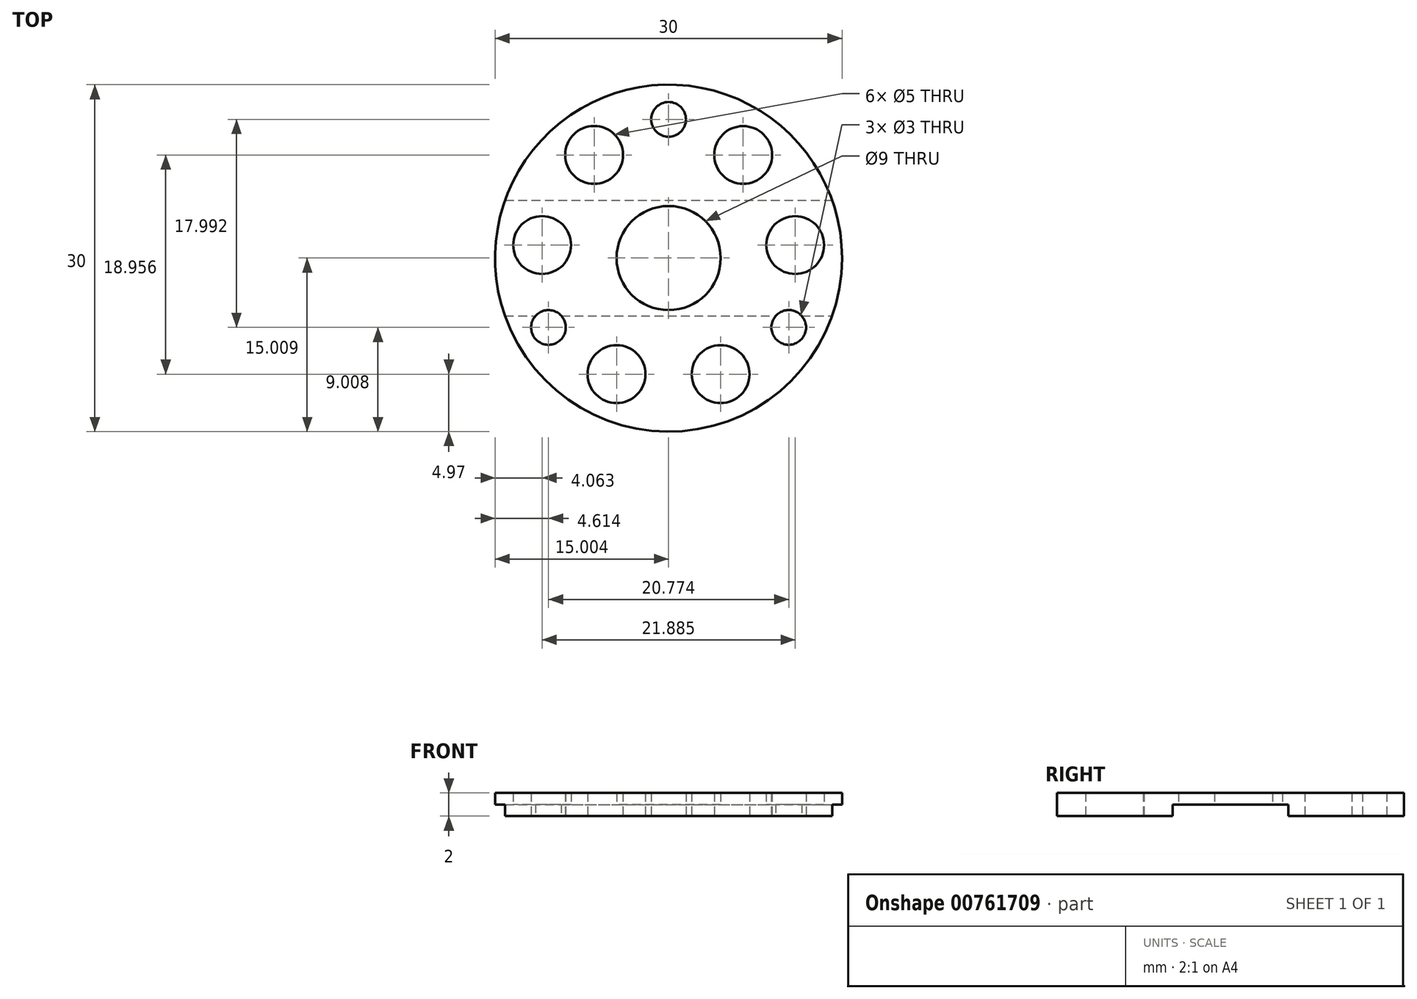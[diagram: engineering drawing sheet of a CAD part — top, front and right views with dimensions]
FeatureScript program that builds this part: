
annotation { "Feature Type Name" : "Feature", "Feature Type Description" : "" }
export const myFeature = defineFeature(function(context is Context, id is Id, definition is map)
    precondition{}
    {
        {
            var Q0;
            Q0=qCreatedBy(makeId("Top.planeOp"),FACE);
            var sketch = newSketch(context, id + "F0", { "sketchPlane" : qUnion([Q0])});
            skCircle(sketch, "E0", {"center": v(0, 0) * mm, "radius": 15 * mm});
            skArc(sketch, "E1", {"start": v(9.57, -7.24) * mm, "mid": v(10.4, -6) * mm, "end": v(11.06, -4.65) * mm, "construction": true});
            skArc(sketch, "E2", {"start": v(4.5, -10.03) * mm, "mid": v(5.6, -9.45) * mm, "end": v(6.65, -8.75) * mm, "construction": true});
            skCircle(sketch, "E3", {"center": v(0, 12) * mm, "radius": 1.5 * mm});
            skCircle(sketch, "E4.1.0", {"center": v(-10.39, -6) * mm, "radius": 1.5 * mm});
            skCircle(sketch, "E4.2.0", {"center": v(10.39, -6) * mm, "radius": 1.5 * mm});
            skLineSegment(sketch, "E4.anchor1", {"start": v(0, 0) * mm, "end": v(0, 12) * mm, "construction": true});
            skLineSegment(sketch, "E4.anchor2", {"start": v(0, 0) * mm, "end": v(3.9, -2.24) * mm, "construction": true});
            skCircle(sketch, "E5", {"center": v(4.5, -10.03) * mm, "radius": 2.5 * mm});
            skCircle(sketch, "E6", {"center": v(-4.5, -10.03) * mm, "radius": 2.5 * mm});
            skLineSegment(sketch, "E7", {"start": v(-4.5, -10.03) * mm, "end": v(-2, -10.03) * mm, "construction": true});
            skCircle(sketch, "E8.1.0", {"center": v(6.45, 8.92) * mm, "radius": 2.5 * mm});
            skCircle(sketch, "E8.1.1", {"center": v(10.95, 1.13) * mm, "radius": 2.5 * mm});
            skCircle(sketch, "E8.2.0", {"center": v(-10.94, 1.14) * mm, "radius": 2.5 * mm});
            skCircle(sketch, "E8.2.1", {"center": v(-6.44, 8.93) * mm, "radius": 2.5 * mm});
            skCircle(sketch, "E9", {"center": v(0, 0) * mm, "radius": 4.5 * mm});
            skLineSegment(sketch, "E10.trimOffspring", {"start": v(2, -10.03) * mm, "end": v(4.5, -10.03) * mm, "construction": true});
            skArc(sketch, "E11.trimOffspring", {"start": v(8.94, -6.4) * mm, "mid": v(9.52, -5.5) * mm, "end": v(10.01, -4.54) * mm, "construction": true});
            skArc(sketch, "E12.trimOffspring", {"start": v(10.9, -1.37) * mm, "mid": v(10.93, 1.13) * mm, "end": v(10.4, 3.57) * mm, "construction": true});
            skArc(sketch, "E13.trimOffspring", {"start": v(11.94, -1.16) * mm, "mid": v(11.94, 1.23) * mm, "end": v(11.45, 3.58) * mm, "construction": true});
            skArc(sketch, "E14.trimOffspring", {"start": v(8.82, 8.13) * mm, "mid": v(7.03, 9.72) * mm, "end": v(4.96, 10.93) * mm, "construction": true});
            skArc(sketch, "E15.trimOffspring", {"start": v(1.5, 11.9) * mm, "mid": v(0, 12) * mm, "end": v(-1.5, 11.9) * mm, "construction": true});
            skArc(sketch, "E16.trimOffspring", {"start": v(1.06, 10.94) * mm, "mid": v(0, 11) * mm, "end": v(-1.06, 10.94) * mm, "construction": true});
            skArc(sketch, "E17.trimOffspring", {"start": v(8.29, 7.22) * mm, "mid": v(6.44, 8.9) * mm, "end": v(4.26, 10.13) * mm, "construction": true});
            skArc(sketch, "E18.trimOffspring", {"start": v(-4.25, 10.14) * mm, "mid": v(-6.43, 8.91) * mm, "end": v(-8.28, 7.23) * mm, "construction": true});
            skArc(sketch, "E19.trimOffspring", {"start": v(-4.95, 10.93) * mm, "mid": v(-7.02, 9.73) * mm, "end": v(-8.81, 8.14) * mm, "construction": true});
            skArc(sketch, "E20.trimOffspring", {"start": v(-10.4, 3.58) * mm, "mid": v(-10.93, 1.14) * mm, "end": v(-10.9, -1.36) * mm, "construction": true});
            skArc(sketch, "E21.trimOffspring", {"start": v(-11.45, 3.58) * mm, "mid": v(-11.94, 1.24) * mm, "end": v(-11.94, -1.15) * mm, "construction": true});
            skArc(sketch, "E22.trimOffspring", {"start": v(-11.06, -4.65) * mm, "mid": v(-10.4, -6) * mm, "end": v(-9.56, -7.25) * mm, "construction": true});
            skArc(sketch, "E23.trimOffspring", {"start": v(-10.01, -4.54) * mm, "mid": v(-9.52, -5.5) * mm, "end": v(-8.94, -6.4) * mm, "construction": true});
            skLineSegment(sketch, "E24.trimOffspring", {"start": v(9.09, -5.24) * mm, "end": v(10.39, -5.99) * mm, "construction": true});
            skCircle(sketch, "E25", {"center": v(0, 0) * mm, "radius": 5 * mm, "construction": true});
            skLineSegment(sketch, "E26", {"start": v(-14.15, -5) * mm, "end": v(14.15, -5) * mm});
            skLineSegment(sketch, "E27", {"start": v(-14.14, 5) * mm, "end": v(14.14, 5) * mm});
            skSolve(sketch);
        }
        {
            var Q0;
            Q0=makeQuery(id+"F0.imprint","IMPRINT",FACE,{"disambiguationData":[TD([[makeQuery(id+"F0.imprint","IMPRINT",EDGE,{"derivedFrom":sQuery(id+"F0.wireOp",EDGE,"E3")}),-1.0]])]});
            var Q1;
            Q1=makeQuery(id+"F0.imprint","IMPRINT",FACE,{"disambiguationData":[TD([[makeQuery(id+"F0.imprint","IMPRINT",EDGE,{"derivedFrom":sQuery(id+"F0.wireOp",EDGE,"E5")}),-1.0]])]});
            var Q2;
            Q2=makeQuery(id+"F0.imprint","IMPRINT",FACE,{"disambiguationData":[TD([[makeQuery(id+"F0.imprint","IMPRINT",EDGE,{"derivedFrom":sQuery(id+"F0.wireOp",EDGE,"E8.1.1")}),-1.0]])]});
            extrude(context, id + "F1", {"entities" : qUnion([Q0, Q1, Q2]), "depth" : 2 * mm, "offsetDistance" : 25 * mm});
        }
        {
            var Q0;
            Q0=makeQuery(id+"F0.imprint","IMPRINT",FACE,{"disambiguationData":[TD([[makeQuery(id+"F0.imprint","IMPRINT",EDGE,{"derivedFrom":sQuery(id+"F0.wireOp",EDGE,"E8.1.1")}),-1.0]])]});
            extrude(context, id + "F2", {"entities" : qUnion([Q0]), "operationType" : NewBodyOperationType.REMOVE, "depth" : 1 * mm, "offsetDistance" : 25 * mm});
        }
    });
